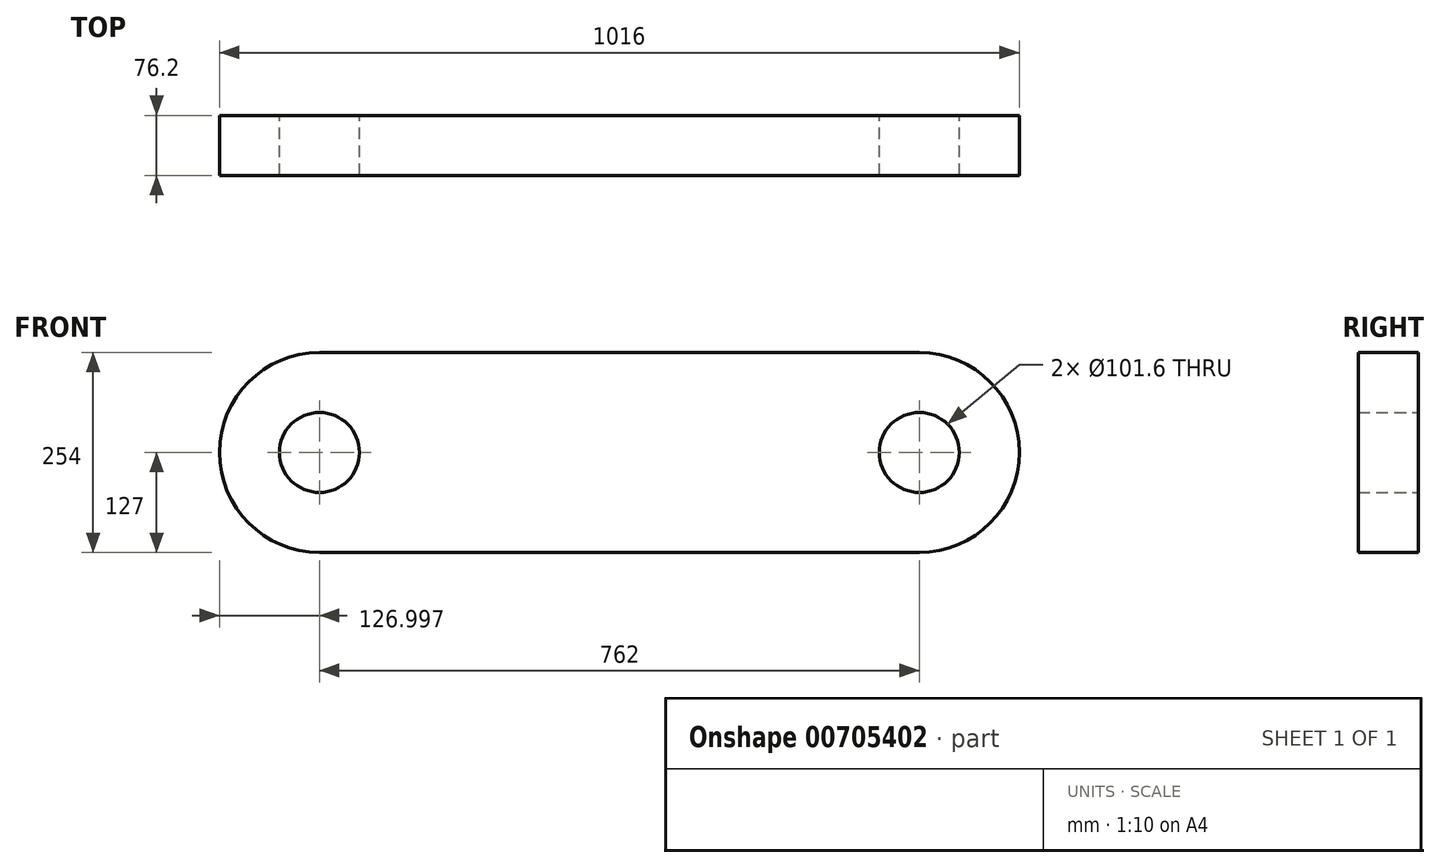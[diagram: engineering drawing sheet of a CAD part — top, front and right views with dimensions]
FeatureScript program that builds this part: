
annotation { "Feature Type Name" : "Feature", "Feature Type Description" : "" }
export const myFeature = defineFeature(function(context is Context, id is Id, definition is map)
    precondition{}
    {
        {
            var Q0;
            Q0=qCreatedBy(makeId("Front.planeOp"),FACE);
            var sketch = newSketch(context, id + "F0", { "sketchPlane" : qUnion([Q0])});
            skLineSegment(sketch, "E0", {"start": v(-712.34, 254) * mm, "end": v(49.66, 254) * mm});
            skLineSegment(sketch, "E1", {"start": v(-712.34, 0) * mm, "end": v(49.66, 0) * mm});
            skArc(sketch, "E2", {"start": v(-712.34, 254) * mm, "mid": v(-839.34, 127) * mm, "end": v(-712.34, 0) * mm});
            skArc(sketch, "E3", {"start": v(49.66, 254) * mm, "mid": v(176.66, 127) * mm, "end": v(49.66, 0) * mm});
            skCircle(sketch, "E4", {"center": v(-712.34, 127) * mm, "radius": 50.8 * mm});
            skCircle(sketch, "E5", {"center": v(49.66, 127) * mm, "radius": 50.8 * mm});
            skSolve(sketch);
        }
        {
            var Q0;
            Q0 = qSketchRegion(id + "F0", true);
            extrude(context, id + "F1", {"entities" : qUnion([Q0]), "depth" : 76.2 * mm, "offsetDistance" : 25.4 * mm});
        }
    });
